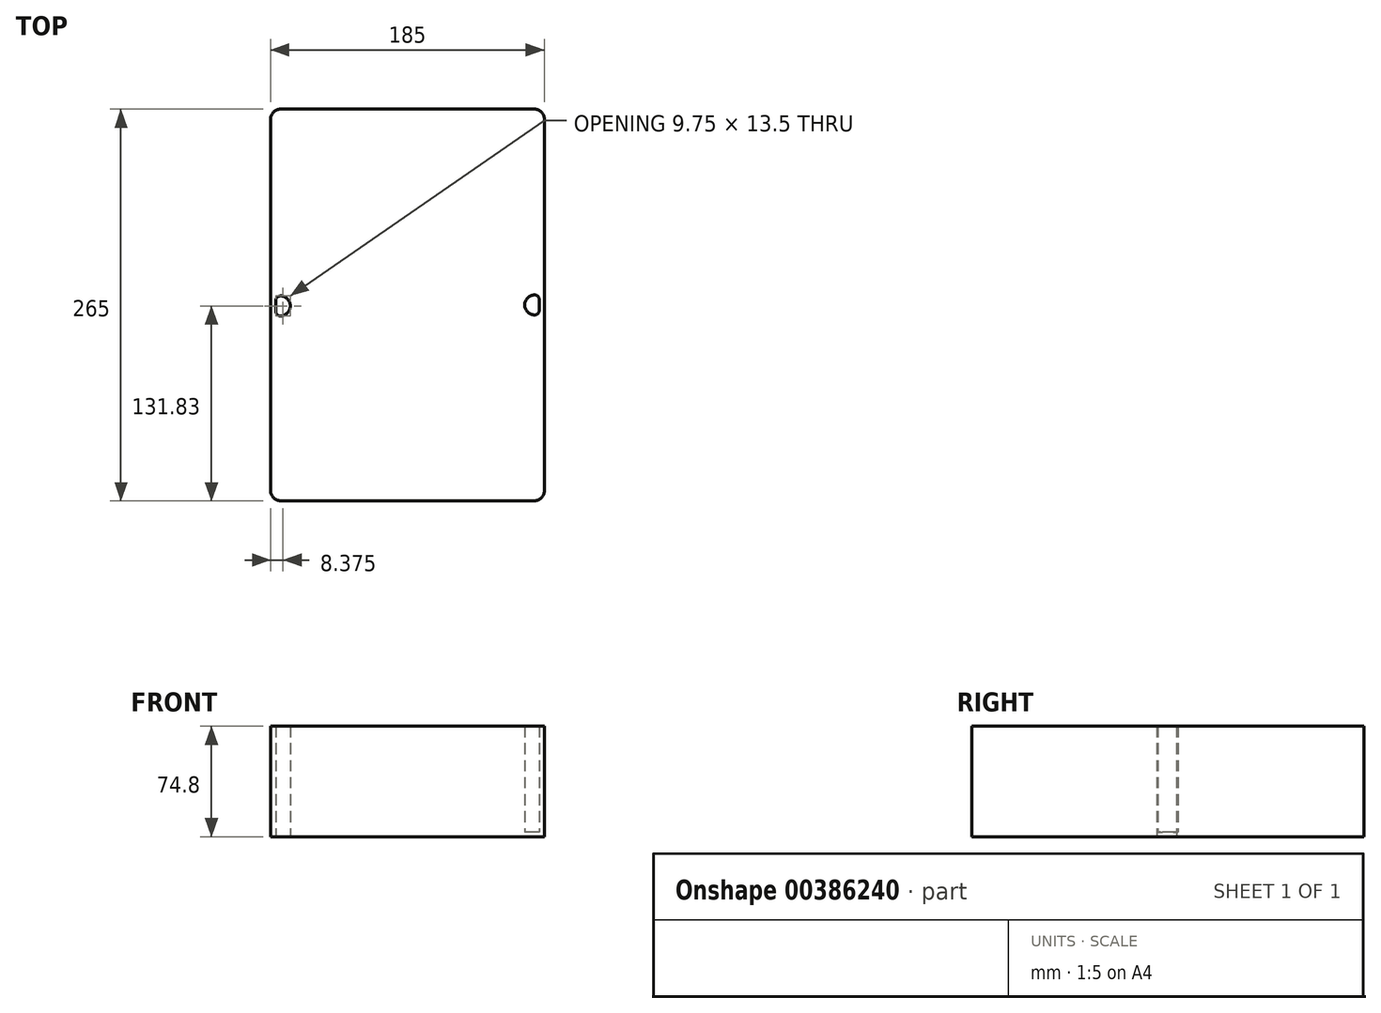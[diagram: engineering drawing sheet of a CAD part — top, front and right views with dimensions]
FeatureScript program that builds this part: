
annotation { "Feature Type Name" : "Feature", "Feature Type Description" : "" }
export const myFeature = defineFeature(function(context is Context, id is Id, definition is map)
    precondition{}
    {
        {
            var Q0;
            Q0=qCreatedBy(makeId("Top.planeOp"),FACE);
            var sketch = newSketch(context, id + "F0", { "sketchPlane" : qUnion([Q0])});
            skLineSegment(sketch, "E0.bottom", {"start": v(92.5, 132.5) * mm, "end": v(-92.5, 132.5) * mm});
            skLineSegment(sketch, "E0.top", {"start": v(92.5, -132.5) * mm, "end": v(-92.5, -132.5) * mm});
            skLineSegment(sketch, "E0.left", {"start": v(92.5, 132.5) * mm, "end": v(92.5, -132.5) * mm});
            skLineSegment(sketch, "E0.right", {"start": v(-92.5, 132.5) * mm, "end": v(-92.5, -132.5) * mm});
            skPoint(sketch, "E0.middle", {"position": v(0, 0) * mm});
            skLineSegment(sketch, "E1.bottom", {"start": v(89, 129) * mm, "end": v(-89, 129) * mm});
            skLineSegment(sketch, "E1.top", {"start": v(89, -129) * mm, "end": v(-89, -129) * mm});
            skLineSegment(sketch, "E1.left", {"start": v(89, 129) * mm, "end": v(89, -129) * mm});
            skLineSegment(sketch, "E1.right", {"start": v(-89, 129) * mm, "end": v(-89, -129) * mm});
            skArc(sketch, "E2", {"start": v(86, -6.75) * mm, "mid": v(79.25, 0) * mm, "end": v(86, 6.75) * mm});
            skLineSegment(sketch, "E3", {"start": v(86, 6.75) * mm, "end": v(89, 6.75) * mm});
            skLineSegment(sketch, "E4", {"start": v(86, -6.75) * mm, "end": v(89, -6.75) * mm});
            skPoint(sketch, "E5.endSnap0", {"position": v(-89, 0) * mm});
            skArc(sketch, "E6", {"start": v(-86, 6.08) * mm, "mid": v(-79.25, -0.67) * mm, "end": v(-86, -7.42) * mm});
            skLineSegment(sketch, "E7", {"start": v(-86, -7.42) * mm, "end": v(-89, -7.42) * mm});
            skLineSegment(sketch, "E8", {"start": v(-86, 6.08) * mm, "end": v(-89, 6.08) * mm});
            skArc(sketch, "E9", {"start": v(-77.35, 119.2) * mm, "mid": v(-72.58, 121.18) * mm, "end": v(-70.6, 125.95) * mm});
            skLineSegment(sketch, "E10", {"start": v(-70.6, 125.95) * mm, "end": v(-70.6, 129) * mm});
            skLineSegment(sketch, "E11", {"start": v(-77.35, 119.2) * mm, "end": v(-89, 119.2) * mm});
            skArc(sketch, "E12", {"start": v(77.35, -119.2) * mm, "mid": v(72.58, -121.18) * mm, "end": v(70.6, -125.95) * mm});
            skLineSegment(sketch, "E13", {"start": v(70.6, -125.95) * mm, "end": v(70.6, -129) * mm});
            skLineSegment(sketch, "E14", {"start": v(77.35, -119.2) * mm, "end": v(89, -119.2) * mm});
            skArc(sketch, "E15", {"start": v(70.6, 125.95) * mm, "mid": v(72.58, 121.18) * mm, "end": v(77.35, 119.2) * mm});
            skLineSegment(sketch, "E16", {"start": v(77.35, 119.2) * mm, "end": v(89, 119.2) * mm});
            skLineSegment(sketch, "E17", {"start": v(70.6, 125.95) * mm, "end": v(70.6, 129) * mm});
            skLineSegment(sketch, "E18", {"start": v(-89, -119.2) * mm, "end": v(-77.35, -119.2) * mm});
            skLineSegment(sketch, "E19", {"start": v(-70.6, -126.2) * mm, "end": v(-70.6, -129) * mm});
            skArc(sketch, "E20", {"start": v(-70.6, -126.2) * mm, "mid": v(-72.48, -121.27) * mm, "end": v(-77.35, -119.2) * mm});
            skSolve(sketch);
        }
        {
            var Q0;
            Q0=makeQuery(id+"F0.imprint","IMPRINT",FACE,{"disambiguationData":[TD([[makeQuery(id+"F0.imprint","IMPRINT",EDGE,{"derivedFrom":sQuery(id+"F0.wireOp",EDGE,"E2")}),1.0]])]});
            extrude(context, id + "F1", {"entities" : qUnion([Q0]), "depth" : 3 * mm, "offsetDistance" : 25 * mm});
        }
        {
            var Q0;
            Q0=makeQuery(id+"F0.imprint","IMPRINT",FACE,{"disambiguationData":[TD([[makeQuery(id+"F0.imprint","IMPRINT",EDGE,{"derivedFrom":sQuery(id+"F0.wireOp",EDGE,"E9")}),1.0]])]});
            var Q1;
            Q1=makeQuery(id+"F0.imprint","IMPRINT",FACE,{"disambiguationData":[TD([[makeQuery(id+"F0.imprint","IMPRINT",EDGE,{"derivedFrom":sQuery(id+"F0.wireOp",EDGE,"E0.bottom")}),1.0]])]});
            var Q2;
            Q2=makeQuery(id+"F0.imprint","IMPRINT",FACE,{"disambiguationData":[TD([[makeQuery(id+"F0.imprint","IMPRINT",EDGE,{"derivedFrom":sQuery(id+"F0.wireOp",EDGE,"E15")}),1.0]])]});
            var Q3;
            Q3=makeQuery(id+"F0.imprint","IMPRINT",FACE,{"disambiguationData":[TD([[makeQuery(id+"F0.imprint","IMPRINT",EDGE,{"derivedFrom":sQuery(id+"F0.wireOp",EDGE,"E6")}),-1.0]])]});
            var Q4;
            Q4=makeQuery(id+"F0.imprint","IMPRINT",FACE,{"disambiguationData":[TD([[makeQuery(id+"F0.imprint","IMPRINT",EDGE,{"derivedFrom":sQuery(id+"F0.wireOp",EDGE,"E2")}),-1.0]])]});
            var Q5;
            {var subQ1=sQuery(id+"F0.wireOp",EDGE,"E18");Q5=makeQuery(id+"F0.imprint","IMPRINT",FACE,{"disambiguationData":[TD([[makeQuery(id+"F0.imprint","IMPRINT",EDGE,{"derivedFrom":subQ1}),-1.0]])]});}
            var Q6;
            Q6=makeQuery(id+"F0.imprint","IMPRINT",FACE,{"disambiguationData":[TD([[makeQuery(id+"F0.imprint","IMPRINT",EDGE,{"derivedFrom":sQuery(id+"F0.wireOp",EDGE,"E12")}),1.0]])]});
            extrude(context, id + "F2", {"entities" : qUnion([Q0, Q1, Q2, Q3, Q4, Q5, Q6]), "operationType" : NewBodyOperationType.ADD, "depth" : 74.8 * mm, "offsetDistance" : 25 * mm});
        }
        {
            var Q0;
            Q0=makeQuery(id+"F2.opExtrude","SWEPT_EDGE",EDGE,{"disambiguationData":[OSD([sQuery(id+"F0.wireOp",EDGE,"E0.bottom"),sQuery(id+"F0.wireOp",EDGE,"E0.right")])]});
            var Q1;
            Q1=makeQuery(id+"F2.opExtrude","SWEPT_EDGE",EDGE,{"disambiguationData":[OSD([sQuery(id+"F0.wireOp",EDGE,"E0.bottom"),sQuery(id+"F0.wireOp",EDGE,"E0.left")])]});
            var Q2;
            Q2=makeQuery(id+"F2.opExtrude","SWEPT_EDGE",EDGE,{"disambiguationData":[OSD([sQuery(id+"F0.wireOp",EDGE,"E0.top"),sQuery(id+"F0.wireOp",EDGE,"E0.left")])]});
            var Q3;
            Q3=makeQuery(id+"F2.opExtrude","SWEPT_EDGE",EDGE,{"disambiguationData":[OSD([sQuery(id+"F0.wireOp",EDGE,"E0.top"),sQuery(id+"F0.wireOp",EDGE,"E0.right")])]});
            fillet(context, id + "F3", {"entities" : qUnion([Q0, Q1, Q2, Q3]), "radius" : 6.75 * mm, "tangentPropagation" : true, "allowEdgeOverflow" : false});
        }
        {
            var Q0;
            Q0=makeQuery(id+"F2.opExtrude","SWEPT_EDGE",EDGE,{"disambiguationData":[OSD([sQuery(id+"F0.wireOp",EDGE,"E1.right"),sQuery(id+"F0.wireOp",EDGE,"E8")])]});
            var Q1;
            Q1=makeQuery(id+"F2.opExtrude","SWEPT_EDGE",EDGE,{"disambiguationData":[OSD([sQuery(id+"F0.wireOp",EDGE,"E1.right"),sQuery(id+"F0.wireOp",EDGE,"E11")])]});
            var Q2;
            Q2=makeQuery(id+"F2.opExtrude","SWEPT_EDGE",EDGE,{"disambiguationData":[OSD([sQuery(id+"F0.wireOp",EDGE,"E1.bottom"),sQuery(id+"F0.wireOp",EDGE,"E10")])]});
            var Q3;
            Q3=makeQuery(id+"F2.opExtrude","SWEPT_EDGE",EDGE,{"disambiguationData":[OSD([sQuery(id+"F0.wireOp",EDGE,"E1.bottom"),sQuery(id+"F0.wireOp",EDGE,"E17")])]});
            var Q4;
            Q4=makeQuery(id+"F2.opExtrude","SWEPT_EDGE",EDGE,{"disambiguationData":[OSD([sQuery(id+"F0.wireOp",EDGE,"E1.left"),sQuery(id+"F0.wireOp",EDGE,"E16")])]});
            var Q5;
            Q5=makeQuery(id+"F2.opExtrude","SWEPT_EDGE",EDGE,{"disambiguationData":[OSD([sQuery(id+"F0.wireOp",EDGE,"E1.right"),sQuery(id+"F0.wireOp",EDGE,"E7")])]});
            var Q6;
            Q6=makeQuery(id+"F2.opExtrude","SWEPT_EDGE",EDGE,{"disambiguationData":[OSD([sQuery(id+"F0.wireOp",EDGE,"E1.left"),sQuery(id+"F0.wireOp",EDGE,"E3")])]});
            var Q7;
            Q7=makeQuery(id+"F2.opExtrude","SWEPT_EDGE",EDGE,{"disambiguationData":[OSD([sQuery(id+"F0.wireOp",EDGE,"E1.left"),sQuery(id+"F0.wireOp",EDGE,"E4")])]});
            var Q8;
            Q8=makeQuery(id+"F2.opExtrude","SWEPT_EDGE",EDGE,{"disambiguationData":[OSD([sQuery(id+"F0.wireOp",EDGE,"E1.right"),sQuery(id+"F0.wireOp",EDGE,"E18")])]});
            var Q9;
            Q9=makeQuery(id+"F2.opExtrude","SWEPT_EDGE",EDGE,{"disambiguationData":[OSD([sQuery(id+"F0.wireOp",EDGE,"E1.top"),sQuery(id+"F0.wireOp",EDGE,"E19")])]});
            var Q10;
            Q10=makeQuery(id+"F2.opExtrude","SWEPT_EDGE",EDGE,{"disambiguationData":[OSD([sQuery(id+"F0.wireOp",EDGE,"E1.top"),sQuery(id+"F0.wireOp",EDGE,"E13")])]});
            var Q11;
            Q11=makeQuery(id+"F2.opExtrude","SWEPT_EDGE",EDGE,{"disambiguationData":[OSD([sQuery(id+"F0.wireOp",EDGE,"E1.left"),sQuery(id+"F0.wireOp",EDGE,"E14")])]});
            fillet(context, id + "F4", {"entities" : qUnion([Q0, Q1, Q2, Q3, Q4, Q5, Q6, Q7, Q8, Q9, Q10, Q11]), "radius" : 3 * mm, "tangentPropagation" : true, "allowEdgeOverflow" : false});
        }
    });
